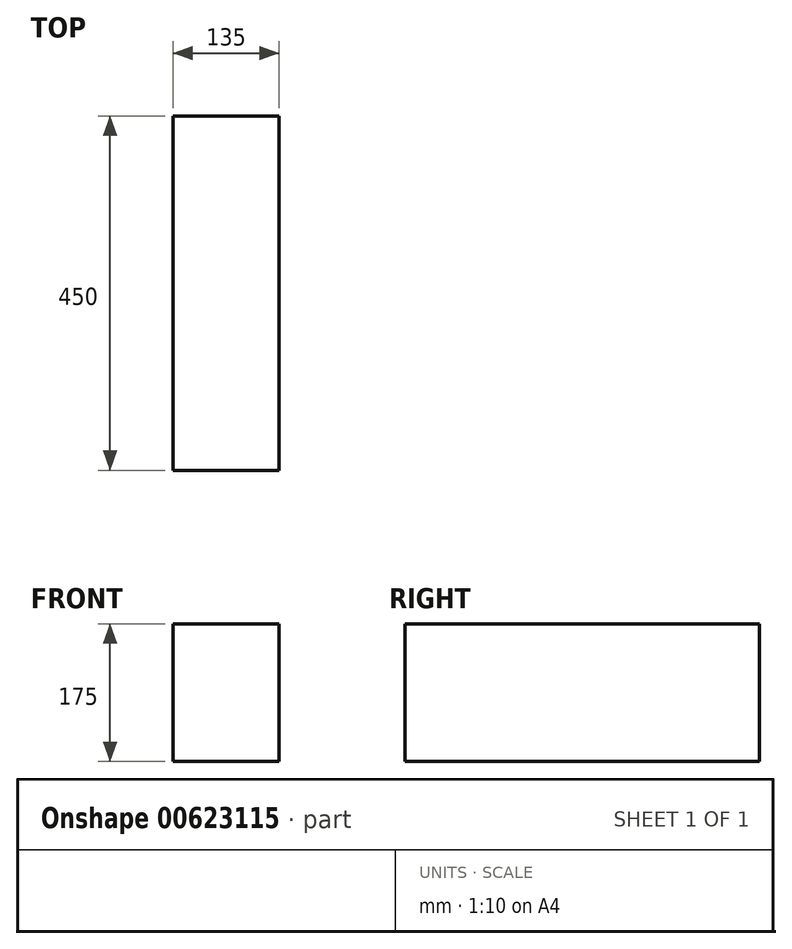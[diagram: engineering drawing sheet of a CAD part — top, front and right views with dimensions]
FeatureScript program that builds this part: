
annotation { "Feature Type Name" : "Feature", "Feature Type Description" : "" }
export const myFeature = defineFeature(function(context is Context, id is Id, definition is map)
    precondition{}
    {
        {
            var Q0;
            Q0=qCreatedBy(makeId("Front.planeOp"),FACE);
            var sketch = newSketch(context, id + "F0", { "sketchPlane" : qUnion([Q0])});
            skLineSegment(sketch, "E0.bottom", {"start": v(0, 0) * mm, "end": v(135, 0) * mm});
            skLineSegment(sketch, "E0.top", {"start": v(0, 175) * mm, "end": v(135, 175) * mm});
            skLineSegment(sketch, "E0.left", {"start": v(0, 0) * mm, "end": v(0, 175) * mm});
            skLineSegment(sketch, "E0.right", {"start": v(135, 0) * mm, "end": v(135, 175) * mm});
            skSolve(sketch);
        }
        {
            var Q0;
            Q0=makeQuery(id+"F0.imprint","IMPRINT",FACE,{"disambiguationData":[TD([[makeQuery(id+"F0.imprint","IMPRINT",EDGE,{"derivedFrom":sQuery(id+"F0.wireOp",EDGE,"E0.bottom")}),1.0]])]});
            extrude(context, id + "F1", {"entities" : qUnion([Q0]), "oppositeDirection" : true, "depth" : 450 * mm, "offsetDistance" : 25.4 * mm});
        }
    });
